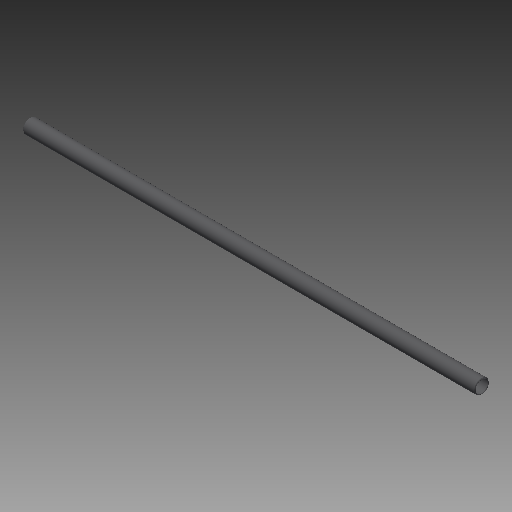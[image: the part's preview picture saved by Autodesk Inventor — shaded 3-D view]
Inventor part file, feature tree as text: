
AUTODESK INVENTOR PART (.ipt)
format: ipt  version: 2018 (Build 220112000, 112)  size: 116,224 bytes
history: native  units: in
note: dims shown in document units (in); Inventor stores cm internally (conversion verified against a paired STEP export)
features: other x42, revolve x1, sketch x1
ambient origin geometry x8: Origin, YZ Plane, XZ Plane, XY Plane, X Axis, Y Axis, Z Axis, Center Point
bodies: Solid1 (feature_tree)
feature tree (44):
  revolve  "Revolution1"  [1 undecoded]
  other  "cp1_XY"
  other  "cp1_YZ"
  other  "cp1_ZX"
  other  "cp1_X"
  other  "cp1_Y"
  other  "cp1_Z"
  other  "cp1_Center"
  other  "cp2_XY"
  other  "cp2_YZ"
  other  "cp2_ZX"
  other  "cp2_X"
  other  "cp2_Y"
  other  "cp2_Z"
  other  "cp2_Center"
  other  "cp3_XY"
  other  "cp3_YZ"
  other  "cp3_ZX"
  other  "cp3_X"
  other  "cp3_Y"
  other  "cp3_Z"
  other  "cp3_Center"
  other  "cp4_XY"
  other  "cp4_YZ"
  other  "cp4_ZX"
  other  "cp4_X"
  other  "cp4_Y"
  other  "cp4_Z"
  other  "cp4_Center"
  other  "tube_front_XY"
  other  "tube_front_YZ"
  other  "tube_front_ZX"
  other  "tube_front_X"
  other  "tube_front_Y"
  other  "tube_front_Z"
  other  "tube_front_Center"
  other  "tube_rear_XY"
  other  "tube_rear_YZ"
  other  "tube_rear_ZX"
  other  "tube_rear_X"
  other  "tube_rear_Y"
  other  "tube_rear_Z"
  other  "tube_rear_Center"
  sketch  "Sketch_1"  dims[d0=360.0deg]
note: 1 required parameter value undecoded (feature->parameter linkage not recoverable at this tier; creation-order binding heuristic only, values carry confidence <= 0.55)
